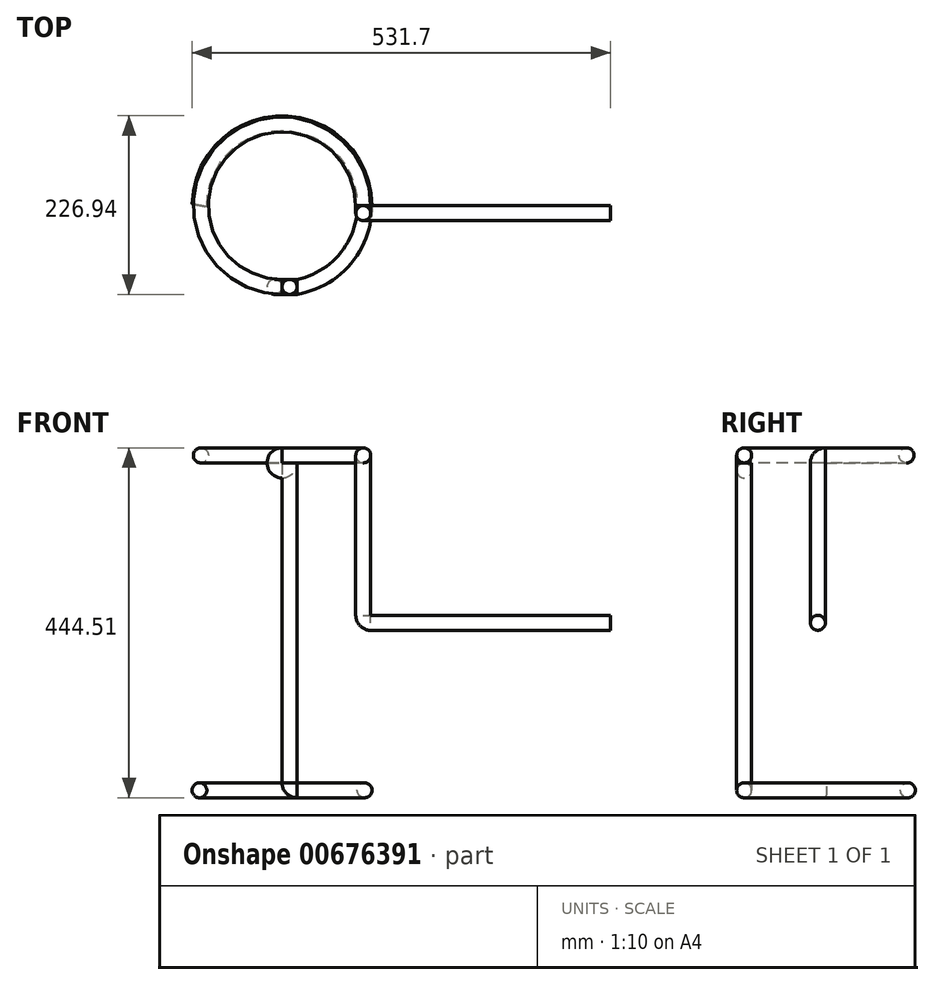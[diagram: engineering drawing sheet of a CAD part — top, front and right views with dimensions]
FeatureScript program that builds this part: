
annotation { "Feature Type Name" : "Feature", "Feature Type Description" : "" }
export const myFeature = defineFeature(function(context is Context, id is Id, definition is map)
    precondition{}
    {
        {
            var Q0;
            Q0=qCreatedBy(makeId("Top.planeOp"),FACE);
            var sketch = newSketch(context, id + "F0", { "sketchPlane" : qUnion([Q0])});
            skArc(sketch, "E0", {"start": v(103.14, 0) * mm, "mid": v(-72.93, 72.93) * mm, "end": v(0, -103.14) * mm});
            skSolve(sketch);
        }
        {
            var Q0;
            Q0=qCreatedBy(makeId("Front.planeOp"),FACE);
            var sketch = newSketch(context, id + "F1", { "sketchPlane" : qUnion([Q0])});
            skCircle(sketch, "E1", {"center": v(103.14, 0) * mm, "radius": 9.53 * mm});
            skSolve(sketch);
        }
        {
            var Q0;
            Q0=makeQuery(id+"F1.imprint","IMPRINT",FACE,{"disambiguationData":[TD([[makeQuery(id+"F1.imprint","IMPRINT",EDGE,{"derivedFrom":sQuery(id+"F1.wireOp",EDGE,"E1")}),1.0]])]});
            var Q1;
            Q1=sQuery(id+"F0.wireOp",EDGE,"E0");
            sweep(context, id + "F2", {"profiles" : qUnion([Q0]), "path" : qUnion([Q1])});
        }
        {
            var Q0;
            Q0=qCreatedBy(makeId("Front.planeOp"),FACE);
            cPlane(context, id + "F3", {"entities" : qUnion([Q0]), "cplaneType" : CPlaneType.OFFSET, "offset" : 103.14 * mm, "width" : 152.4 * mm, "height" : 152.4 * mm});
        }
        {
            var Q0;
            Q0=qCreatedBy(id+"F3.planeOp",FACE);
            var sketch = newSketch(context, id + "F4", { "sketchPlane" : qUnion([Q0])});
            skArc(sketch, "E2", {"start": v(9.53, -9.53) * mm, "mid": v(6.74, -2.79) * mm, "end": v(0, 0) * mm});
            skLineSegment(sketch, "E3", {"start": v(9.53, -9.53) * mm, "end": v(9.53, -415.93) * mm});
            skSolve(sketch);
        }
        {
            var Q0;
            Q0=makeQuery(id+"F2.opSweep","CAP_FACE",FACE,{"disambiguationData":[OSD([sQuery(id+"F0.wireOp",VERTEX,"E0.end"),sQuery(id+"F1.wireOp",EDGE,"E1")])],"isStart":false});
            var Q1;
            Q1=sQuery(id+"F4.wireOp",EDGE,"E2");
            var Q2;
            Q2=sQuery(id+"F4.wireOp",EDGE,"E3");
            sweep(context, id + "F5", {"operationType" : NewBodyOperationType.ADD, "profiles" : qUnion([Q0]), "path" : qUnion([Q1, Q2])});
        }
        {
            var Q0;
            Q0=qCreatedBy(id+"F3.planeOp",FACE);
            var sketch = newSketch(context, id + "F6", { "sketchPlane" : qUnion([Q0])});
            skLineSegment(sketch, "E4", {"start": v(9.53, -188.55) * mm, "end": v(9.53, -415.93) * mm, "construction": true});
            skArc(sketch, "E5.MirrorCS", {"start": v(19.05, -425.45) * mm, "mid": v(12.31, -422.66) * mm, "end": v(9.53, -415.93) * mm});
            skLineSegment(sketch, "E6", {"start": v(9.53, -415.93) * mm, "end": v(9.53, 0) * mm, "construction": true});
            skLineSegment(sketch, "E7", {"start": v(9.53, -415.93) * mm, "end": v(0, -415.93) * mm, "construction": true});
            skLineSegment(sketch, "E8", {"start": v(0, -415.93) * mm, "end": v(0, 0) * mm, "construction": true});
            skLineSegment(sketch, "E9", {"start": v(0, 0) * mm, "end": v(9.53, 0) * mm, "construction": true});
            skSolve(sketch);
        }
        {
            var Q0;
            Q0=qCreatedBy(makeId("Top.planeOp"),FACE);
            cPlane(context, id + "F7", {"entities" : qUnion([Q0]), "cplaneType" : CPlaneType.OFFSET, "offset" : 425.45 * mm, "oppositeDirection" : true, "width" : 152.4 * mm, "height" : 152.4 * mm});
        }
        {
            var Q0;
            Q0=qCreatedBy(id+"F7.planeOp",FACE);
            var sketch = newSketch(context, id + "F8", { "sketchPlane" : qUnion([Q0])});
            skArc(sketch, "E10", {"start": v(18.96, -101.38) * mm, "mid": v(65.89, 79.35) * mm, "end": v(-103.14, 0) * mm});
            skLineSegment(sketch, "E11", {"start": v(0, 0) * mm, "end": v(25.16, -100.02) * mm});
            skSolve(sketch);
        }
        {
            var Q0;
            Q0=qCreatedBy(makeId("Right.planeOp"),FACE);
            cPlane(context, id + "F9", {"entities" : qUnion([Q0]), "cplaneType" : CPlaneType.OFFSET, "offset" : 103.14 * mm, "width" : 152.4 * mm, "height" : 152.4 * mm});
        }
        {
            var Q0;
            Q0=qCreatedBy(id+"F9.planeOp",FACE);
            var sketch = newSketch(context, id + "F10", { "sketchPlane" : qUnion([Q0])});
            skArc(sketch, "E12", {"start": v(0, 0) * mm, "mid": v(-6.74, -2.79) * mm, "end": v(-9.53, -9.52) * mm});
            skLineSegment(sketch, "E13", {"start": v(0, -9.53) * mm, "end": v(0, 0) * mm, "construction": true});
            skLineSegment(sketch, "E14", {"start": v(0, 0) * mm, "end": v(0, -9.53) * mm, "construction": true});
            skLineSegment(sketch, "E15", {"start": v(-9.53, -9.52) * mm, "end": v(-9.52, -203.2) * mm});
            skSolve(sketch);
        }
        {
            var Q0;
            Q0=makeQuery(id+"F5.opSweep","CAP_FACE",FACE,{"disambiguationData":[OSD([sQuery(id+"F0.wireOp",VERTEX,"E0.end"),sQuery(id+"F1.wireOp",EDGE,"E1"),sQuery(id+"F4.wireOp",VERTEX,"E3.end")])],"isStart":false});
            var Q1;
            Q1=sQuery(id+"F6.wireOp",EDGE,"E5.MirrorCS");
            sweep(context, id + "F11", {"operationType" : NewBodyOperationType.ADD, "profiles" : qUnion([Q0]), "path" : qUnion([Q1])});
        }
        {
            var Q0;
            Q0=makeQuery(id+"F11.opSweep","CAP_FACE",FACE,{"disambiguationData":[OSD([sQuery(id+"F0.wireOp",VERTEX,"E0.end"),sQuery(id+"F1.wireOp",EDGE,"E1"),sQuery(id+"F4.wireOp",VERTEX,"E3.end"),sQuery(id+"F6.wireOp",VERTEX,"E5.MirrorCS.start")])],"isStart":false});
            var Q1;
            Q1=sQuery(id+"F8.wireOp",EDGE,"E10");
            sweep(context, id + "F12", {"operationType" : NewBodyOperationType.ADD, "profiles" : qUnion([Q0]), "path" : qUnion([Q1])});
        }
        {
            var Q0;
            Q0=makeQuery(id+"F2.opSweep","CAP_FACE",FACE,{"disambiguationData":[OSD([sQuery(id+"F0.wireOp",VERTEX,"E0.start"),sQuery(id+"F1.wireOp",EDGE,"E1")])],"isStart":true});
            var Q1;
            Q1=sQuery(id+"F10.wireOp",EDGE,"E12");
            var Q2;
            Q2=sQuery(id+"F10.wireOp",EDGE,"E15");
            sweep(context, id + "F13", {"profiles" : qUnion([Q0]), "path" : qUnion([Q1, Q2])});
        }
        {
            var Q0;
            Q0=qCreatedBy(makeId("Front.planeOp"),FACE);
            var sketch = newSketch(context, id + "F14", { "sketchPlane" : qUnion([Q0])});
            skLineSegment(sketch, "E16", {"start": v(0, 0) * mm, "end": v(103.14, 0) * mm, "construction": true});
            skLineSegment(sketch, "E17", {"start": v(103.14, 0) * mm, "end": v(103.14, -203.2) * mm, "construction": true});
            skArc(sketch, "E18", {"start": v(103.14, -203.2) * mm, "mid": v(105.93, -209.94) * mm, "end": v(112.66, -212.73) * mm});
            skLineSegment(sketch, "E19", {"start": v(112.66, -203.2) * mm, "end": v(103.14, -203.2) * mm, "construction": true});
            skLineSegment(sketch, "E20", {"start": v(112.66, -212.72) * mm, "end": v(417.46, -212.72) * mm});
            skSolve(sketch);
        }
        {
            var Q0;
            Q0=makeQuery(id+"F13.opSweep","CAP_FACE",FACE,{"disambiguationData":[OSD([sQuery(id+"F0.wireOp",VERTEX,"E0.start"),sQuery(id+"F1.wireOp",EDGE,"E1"),sQuery(id+"F10.wireOp",VERTEX,"E15.end")])],"isStart":false});
            var Q1;
            Q1=sQuery(id+"F14.wireOp",EDGE,"E18");
            var Q2;
            Q2=sQuery(id+"F14.wireOp",EDGE,"E20");
            sweep(context, id + "F15", {"operationType" : NewBodyOperationType.ADD, "profiles" : qUnion([Q0]), "path" : qUnion([Q1, Q2])});
        }
    });
